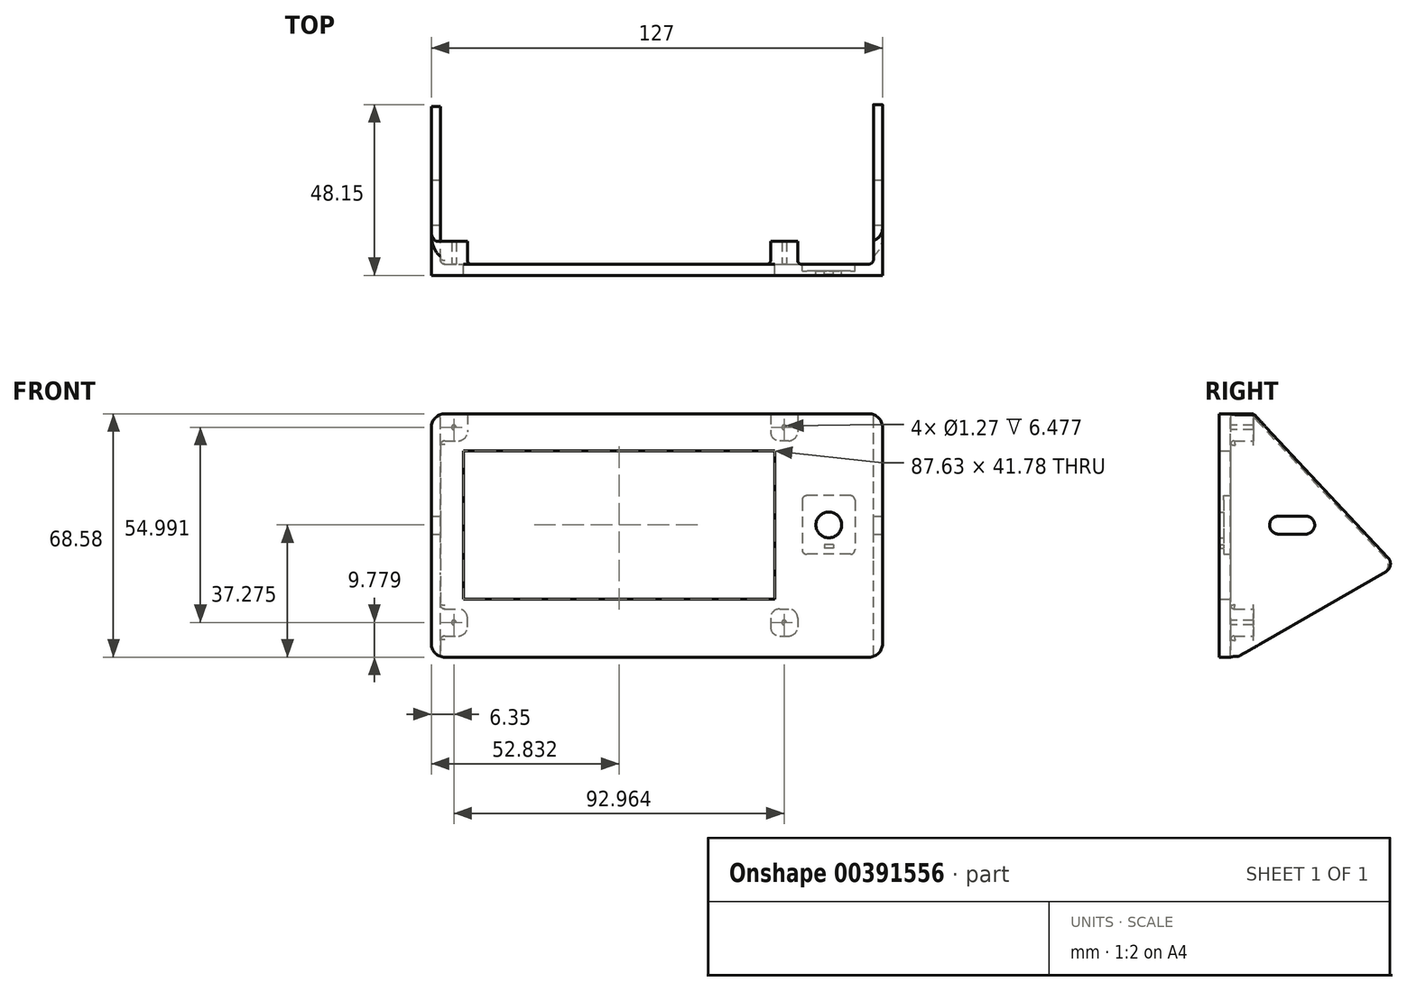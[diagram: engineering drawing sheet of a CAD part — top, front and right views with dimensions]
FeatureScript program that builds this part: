
annotation { "Feature Type Name" : "Feature", "Feature Type Description" : "" }
export const myFeature = defineFeature(function(context is Context, id is Id, definition is map)
    precondition{}
    {
        {
            var Q0;
            Q0=qCreatedBy(makeId("Front.planeOp"),FACE);
            var sketch = newSketch(context, id + "F0", { "sketchPlane" : qUnion([Q0])});
            skLineSegment(sketch, "E0.bottom", {"start": v(5.08, 2.54) * mm, "end": v(127, 2.54) * mm});
            skLineSegment(sketch, "E0.top", {"start": v(5.08, 71.12) * mm, "end": v(127, 71.12) * mm});
            skLineSegment(sketch, "E0.left", {"start": v(2.54, 5.08) * mm, "end": v(2.54, 68.58) * mm});
            skLineSegment(sketch, "E0.right", {"start": v(129.54, 5.08) * mm, "end": v(129.54, 68.58) * mm});
            skPoint(sketch, "E1.visualSharp", {"position": v(2.54, 2.54) * mm});
            skArc(sketch, "E1.filletArc", {"start": v(2.54, 5.08) * mm, "mid": v(3.28, 3.28) * mm, "end": v(5.08, 2.54) * mm});
            skPoint(sketch, "E2.visualSharp", {"position": v(2.54, 71.12) * mm});
            skArc(sketch, "E2.filletArc", {"start": v(5.08, 71.12) * mm, "mid": v(3.28, 70.38) * mm, "end": v(2.54, 68.58) * mm});
            skPoint(sketch, "E3.visualSharp", {"position": v(129.54, 71.12) * mm});
            skArc(sketch, "E3.filletArc", {"start": v(129.54, 68.58) * mm, "mid": v(128.8, 70.38) * mm, "end": v(127, 71.12) * mm});
            skPoint(sketch, "E4.visualSharp", {"position": v(129.54, 2.54) * mm});
            skArc(sketch, "E4.filletArc", {"start": v(127, 2.54) * mm, "mid": v(128.8, 3.28) * mm, "end": v(129.54, 5.08) * mm});
            skSolve(sketch);
        }
        {
            var Q0;
            Q0 = qSketchRegion(id + "F0", true);
            extrude(context, id + "F1", {"entities" : qUnion([Q0]), "oppositeDirection" : true, "depth" : 3.17 * mm, "offsetDistance" : 25.4 * mm});
        }
        {
            var Q0;
            Q0=makeQuery(id+"F1.opExtrude","CAP_FACE",FACE,{"disambiguationData":[OSD([sQuery(id+"F0.wireOp",EDGE,"E0.bottom"),sQuery(id+"F0.wireOp",EDGE,"E0.top"),sQuery(id+"F0.wireOp",EDGE,"E0.left"),sQuery(id+"F0.wireOp",EDGE,"E0.right")])],"isStart":false});
            var sketch = newSketch(context, id + "F2", { "sketchPlane" : qUnion([Q0])});
            skLineSegment(sketch, "E5.bottom", {"start": v(-5.08, 71.12) * mm, "end": v(-12.7, 71.12) * mm});
            skLineSegment(sketch, "E5.top", {"start": v(-2.54, 63.5) * mm, "end": v(-10.16, 63.5) * mm});
            skLineSegment(sketch, "E5.left", {"start": v(-2.54, 68.58) * mm, "end": v(-2.54, 63.5) * mm});
            skLineSegment(sketch, "E5.right", {"start": v(-12.7, 71.12) * mm, "end": v(-12.7, 66.04) * mm});
            skLineSegment(sketch, "E6.bottom", {"start": v(-105.66, 71.12) * mm, "end": v(-98.04, 71.12) * mm});
            skLineSegment(sketch, "E6.top", {"start": v(-103.12, 63.5) * mm, "end": v(-100.58, 63.5) * mm});
            skLineSegment(sketch, "E6.left", {"start": v(-105.66, 71.12) * mm, "end": v(-105.66, 66.04) * mm});
            skLineSegment(sketch, "E6.right", {"start": v(-98.04, 71.12) * mm, "end": v(-98.04, 66.04) * mm});
            skLineSegment(sketch, "E7.bottom", {"start": v(-2.54, 8.5) * mm, "end": v(-10.16, 8.5) * mm});
            skLineSegment(sketch, "E7.top", {"start": v(-2.54, 16.13) * mm, "end": v(-10.16, 16.13) * mm});
            skLineSegment(sketch, "E7.left", {"start": v(-2.54, 8.5) * mm, "end": v(-2.54, 16.13) * mm});
            skLineSegment(sketch, "E7.right", {"start": v(-12.7, 11.05) * mm, "end": v(-12.7, 13.59) * mm});
            skLineSegment(sketch, "E8.bottom", {"start": v(-100.58, 16.13) * mm, "end": v(-103.12, 16.13) * mm});
            skLineSegment(sketch, "E8.top", {"start": v(-100.58, 8.5) * mm, "end": v(-103.12, 8.5) * mm});
            skLineSegment(sketch, "E8.left", {"start": v(-98.04, 13.59) * mm, "end": v(-98.04, 11.05) * mm});
            skLineSegment(sketch, "E8.right", {"start": v(-105.66, 13.59) * mm, "end": v(-105.66, 11.05) * mm});
            skCircle(sketch, "E9", {"center": v(-8.89, 67.31) * mm, "radius": 0.64 * mm});
            skCircle(sketch, "E10", {"center": v(-101.85, 67.31) * mm, "radius": 0.64 * mm});
            skCircle(sketch, "E11", {"center": v(-101.85, 12.32) * mm, "radius": 0.64 * mm});
            skCircle(sketch, "E12", {"center": v(-8.89, 12.32) * mm, "radius": 0.64 * mm});
            skPoint(sketch, "E13.visualSharp", {"position": v(-2.54, 71.12) * mm});
            skArc(sketch, "E13.filletArc", {"start": v(-2.54, 68.58) * mm, "mid": v(-3.28, 70.38) * mm, "end": v(-5.08, 71.12) * mm});
            skPoint(sketch, "E14.visualSharp", {"position": v(-12.7, 63.5) * mm});
            skArc(sketch, "E14.filletArc", {"start": v(-12.7, 66.04) * mm, "mid": v(-11.96, 64.24) * mm, "end": v(-10.16, 63.5) * mm});
            skPoint(sketch, "E15.visualSharp", {"position": v(-105.66, 63.5) * mm});
            skArc(sketch, "E15.filletArc", {"start": v(-105.66, 66.04) * mm, "mid": v(-104.92, 64.24) * mm, "end": v(-103.12, 63.5) * mm});
            skPoint(sketch, "E16.visualSharp", {"position": v(-98.04, 63.5) * mm});
            skArc(sketch, "E16.filletArc", {"start": v(-100.58, 63.5) * mm, "mid": v(-98.79, 64.24) * mm, "end": v(-98.04, 66.04) * mm});
            skPoint(sketch, "E17.visualSharp", {"position": v(-98.04, 16.13) * mm});
            skArc(sketch, "E17.filletArc", {"start": v(-98.04, 13.59) * mm, "mid": v(-98.79, 15.39) * mm, "end": v(-100.58, 16.13) * mm});
            skPoint(sketch, "E18.visualSharp", {"position": v(-98.04, 8.5) * mm});
            skArc(sketch, "E18.filletArc", {"start": v(-100.58, 8.5) * mm, "mid": v(-98.79, 9.25) * mm, "end": v(-98.04, 11.05) * mm});
            skPoint(sketch, "E19.visualSharp", {"position": v(-105.66, 8.5) * mm});
            skArc(sketch, "E19.filletArc", {"start": v(-105.66, 11.05) * mm, "mid": v(-104.92, 9.25) * mm, "end": v(-103.12, 8.5) * mm});
            skPoint(sketch, "E20.visualSharp", {"position": v(-105.66, 16.13) * mm});
            skArc(sketch, "E20.filletArc", {"start": v(-103.12, 16.13) * mm, "mid": v(-104.92, 15.39) * mm, "end": v(-105.66, 13.59) * mm});
            skPoint(sketch, "E21.visualSharp", {"position": v(-12.7, 8.5) * mm});
            skArc(sketch, "E21.filletArc", {"start": v(-12.7, 11.05) * mm, "mid": v(-11.96, 9.25) * mm, "end": v(-10.16, 8.5) * mm});
            skPoint(sketch, "E22.visualSharp", {"position": v(-12.7, 16.13) * mm});
            skArc(sketch, "E22.filletArc", {"start": v(-10.16, 16.13) * mm, "mid": v(-11.96, 15.39) * mm, "end": v(-12.7, 13.59) * mm});
            skSolve(sketch);
        }
        {
            var Q0;
            Q0 = qSketchRegion(id + "F2", true);
            extrude(context, id + "F3", {"entities" : qUnion([Q0]), "operationType" : NewBodyOperationType.ADD, "depth" : 6.48 * mm, "offsetDistance" : 25.4 * mm});
        }
        {
            var Q0;
            Q0=makeQuery(id+"F3.boolean.opBoolean","MERGE",FACE,{"derivedFrom":[makeQuery(id+"F1.opExtrude","SWEPT_FACE",FACE,{"disambiguationData":[OSD([sQuery(id+"F0.wireOp",EDGE,"E0.left")])]}),makeQuery(id+"F3.opExtrude","SWEPT_FACE",FACE,{"disambiguationData":[OSD([sQuery(id+"F2.wireOp",EDGE,"E5.left")])]}),makeQuery(id+"F3.opExtrude","SWEPT_FACE",FACE,{"disambiguationData":[OSD([sQuery(id+"F2.wireOp",EDGE,"E7.left")])]})]});
            var sketch = newSketch(context, id + "F4", { "sketchPlane" : qUnion([Q0])});
            skLineSegment(sketch, "E23", {"start": v(0, 2.54) * mm, "end": v(-5.08, 2.54) * mm});
            skLineSegment(sketch, "E24", {"start": v(-5.08, 2.54) * mm, "end": v(-46.3, 26.34) * mm});
            skLineSegment(sketch, "E25", {"start": v(-46.9, 30.28) * mm, "end": v(-8.76, 71.12) * mm});
            skLineSegment(sketch, "E26", {"start": v(0, 71.12) * mm, "end": v(0, 2.54) * mm});
            skPoint(sketch, "E27.visualSharp", {"position": v(-49.07, 27.94) * mm});
            skArc(sketch, "E27.filletArc", {"start": v(-46.9, 30.28) * mm, "mid": v(-47.55, 28.17) * mm, "end": v(-46.3, 26.34) * mm});
            skLineSegment(sketch, "E28", {"start": v(-8.76, 71.12) * mm, "end": v(0, 71.12) * mm});
            skSolve(sketch);
        }
        {
            var Q0;
            Q0 = qSketchRegion(id + "F4", true);
            extrude(context, id + "F5", {"entities" : qUnion([Q0]), "operationType" : NewBodyOperationType.ADD, "oppositeDirection" : true, "depth" : 2.54 * mm, "offsetDistance" : 25.4 * mm});
        }
        {
            var Q0;
            Q0=makeQuery(id+"F1.opExtrude","SWEPT_FACE",FACE,{"disambiguationData":[OSD([sQuery(id+"F0.wireOp",EDGE,"E0.right")])]});
            var sketch = newSketch(context, id + "F6", { "sketchPlane" : qUnion([Q0])});
            skLineSegment(sketch, "E29", {"start": v(0, 2.54) * mm, "end": v(5.08, 2.54) * mm});
            skPoint(sketch, "E29.startSnap0", {"position": v(1.59, 5.08) * mm});
            skLineSegment(sketch, "E30", {"start": v(5.08, 2.54) * mm, "end": v(46.88, 26.68) * mm});
            skLineSegment(sketch, "E31", {"start": v(47.47, 30.6) * mm, "end": v(9.65, 71.12) * mm});
            skLineSegment(sketch, "E32", {"start": v(9.65, 71.12) * mm, "end": v(0, 71.12) * mm});
            skLineSegment(sketch, "E33", {"start": v(0, 71.12) * mm, "end": v(0, 2.54) * mm});
            skPoint(sketch, "E34.visualSharp", {"position": v(49.65, 28.27) * mm});
            skArc(sketch, "E34.filletArc", {"start": v(46.88, 26.68) * mm, "mid": v(48.13, 28.5) * mm, "end": v(47.47, 30.6) * mm});
            skSolve(sketch);
        }
        {
            var Q0;
            Q0 = qSketchRegion(id + "F6", true);
            extrude(context, id + "F7", {"entities" : qUnion([Q0]), "operationType" : NewBodyOperationType.ADD, "oppositeDirection" : true, "depth" : 2.54 * mm, "offsetDistance" : 25.4 * mm});
        }
        {
            var Q0;
            {var subQ0=sQuery(id+"F0.wireOp",EDGE,"E0.top");var subQ1=sQuery(id+"F0.wireOp",EDGE,"E0.right");var subQ2=sQuery(id+"F0.wireOp",EDGE,"E0.bottom");var subQ3=sQuery(id+"F0.wireOp",EDGE,"E1.filletArc");var subQ4=sQuery(id+"F0.wireOp",EDGE,"E3.filletArc");var subQ5=sQuery(id+"F0.wireOp",EDGE,"E4.filletArc");var subQ6=sQuery(id+"F0.wireOp",EDGE,"E0.left");Q0=makeQuery(id+"F3.boolean.opBoolean","SPLIT",FACE,{"disambiguationData":[TD([makeQuery(id+"F1.opExtrude","SWEPT_FACE",FACE,{"disambiguationData":[OSD([subQ2])]})])],"derivedFrom":makeQuery(id+"F1.opExtrude","CAP_FACE",FACE,{"disambiguationData":[OSD([subQ2,subQ0,subQ6,subQ1,subQ3,sQuery(id+"F0.wireOp",EDGE,"E2.filletArc"),subQ4,subQ5])],"isStart":false})});}
            var sketch = newSketch(context, id + "F8", { "sketchPlane" : qUnion([Q0])});
            skLineSegment(sketch, "E35.bottom", {"start": v(-99.19, 60.7) * mm, "end": v(-11.56, 60.7) * mm});
            skLineSegment(sketch, "E35.top", {"start": v(-99.19, 18.92) * mm, "end": v(-11.56, 18.92) * mm});
            skLineSegment(sketch, "E35.left", {"start": v(-99.19, 60.7) * mm, "end": v(-99.19, 18.92) * mm});
            skLineSegment(sketch, "E35.right", {"start": v(-11.56, 60.7) * mm, "end": v(-11.56, 18.92) * mm});
            skCircle(sketch, "E36", {"center": v(-114.43, 39.8) * mm, "radius": 3.62 * mm});
            skLineSegment(sketch, "E37", {"start": v(-114.43, 30.47) * mm, "end": v(-114.43, 45.35) * mm, "construction": true});
            skSolve(sketch);
        }
        {
            var Q0;
            Q0 = qSketchRegion(id + "F8", true);
            extrude(context, id + "F9", {"entities" : qUnion([Q0]), "operationType" : NewBodyOperationType.REMOVE, "endBound" : BoundingType.UP_TO_NEXT, "oppositeDirection" : true, "depth" : 25.4 * mm, "offsetDistance" : 25.4 * mm});
        }
        {
            var Q0;
            {var subQ0=sQuery(id+"F0.wireOp",EDGE,"E0.top");var subQ1=sQuery(id+"F0.wireOp",EDGE,"E0.right");var subQ2=sQuery(id+"F0.wireOp",EDGE,"E0.bottom");var subQ3=sQuery(id+"F0.wireOp",EDGE,"E1.filletArc");var subQ4=sQuery(id+"F0.wireOp",EDGE,"E3.filletArc");var subQ5=sQuery(id+"F0.wireOp",EDGE,"E4.filletArc");var subQ6=sQuery(id+"F0.wireOp",EDGE,"E0.left");Q0=makeQuery(id+"F3.boolean.opBoolean","SPLIT",FACE,{"disambiguationData":[TD([makeQuery(id+"F1.opExtrude","SWEPT_FACE",FACE,{"disambiguationData":[OSD([subQ2])]})])],"derivedFrom":makeQuery(id+"F1.opExtrude","CAP_FACE",FACE,{"disambiguationData":[OSD([subQ2,subQ0,subQ6,subQ1,subQ3,sQuery(id+"F0.wireOp",EDGE,"E2.filletArc"),subQ4,subQ5])],"isStart":false})});}
            var sketch = newSketch(context, id + "F10", { "sketchPlane" : qUnion([Q0])});
            skLineSegment(sketch, "E38.bottom", {"start": v(-120.52, 48.06) * mm, "end": v(-108.2, 48.06) * mm});
            skLineSegment(sketch, "E38.top", {"start": v(-120.52, 31.55) * mm, "end": v(-108.2, 31.55) * mm});
            skLineSegment(sketch, "E38.left", {"start": v(-121.8, 46.79) * mm, "end": v(-121.8, 32.82) * mm});
            skLineSegment(sketch, "E38.right", {"start": v(-106.93, 46.79) * mm, "end": v(-106.93, 32.82) * mm});
            skPoint(sketch, "E39.visualSharp", {"position": v(-106.93, 31.55) * mm});
            skArc(sketch, "E39.filletArc", {"start": v(-108.2, 31.55) * mm, "mid": v(-107.3, 31.92) * mm, "end": v(-106.93, 32.82) * mm});
            skPoint(sketch, "E40.visualSharp", {"position": v(-106.93, 48.06) * mm});
            skArc(sketch, "E40.filletArc", {"start": v(-106.93, 46.79) * mm, "mid": v(-107.3, 47.68) * mm, "end": v(-108.2, 48.06) * mm});
            skPoint(sketch, "E41.visualSharp", {"position": v(-121.8, 48.06) * mm});
            skArc(sketch, "E41.filletArc", {"start": v(-120.52, 48.06) * mm, "mid": v(-121.42, 47.68) * mm, "end": v(-121.8, 46.79) * mm});
            skPoint(sketch, "E42.visualSharp", {"position": v(-121.8, 31.55) * mm});
            skArc(sketch, "E42.filletArc", {"start": v(-121.8, 32.82) * mm, "mid": v(-121.42, 31.92) * mm, "end": v(-120.52, 31.55) * mm});
            skSolve(sketch);
        }
        {
            var Q0;
            Q0 = qSketchRegion(id + "F10", true);
            extrude(context, id + "F11", {"entities" : qUnion([Q0]), "operationType" : NewBodyOperationType.REMOVE, "oppositeDirection" : true, "depth" : 1.9 * mm, "offsetDistance" : 25.4 * mm});
        }
        {
            var Q0;
            Q0=makeQuery(id+"F11.boolean.opBoolean","COPY",FACE,{"derivedFrom":makeQuery(id+"F11.opExtrude","CAP_FACE",FACE,{"disambiguationData":[OSD([sQuery(id+"F10.wireOp",EDGE,"E38.bottom"),sQuery(id+"F10.wireOp",EDGE,"E38.top"),sQuery(id+"F10.wireOp",EDGE,"E38.left"),sQuery(id+"F10.wireOp",EDGE,"E38.right"),sQuery(id+"F10.wireOp",EDGE,"E39.filletArc"),sQuery(id+"F10.wireOp",EDGE,"E40.filletArc"),sQuery(id+"F10.wireOp",EDGE,"E41.filletArc"),sQuery(id+"F10.wireOp",EDGE,"E42.filletArc")])],"isStart":false})});
            var sketch = newSketch(context, id + "F12", { "sketchPlane" : qUnion([Q0])});
            skLineSegment(sketch, "E43.bottom", {"start": v(-115.7, 34.28) * mm, "end": v(-113.16, 34.28) * mm});
            skLineSegment(sketch, "E43.top", {"start": v(-115.7, 33.27) * mm, "end": v(-113.16, 33.27) * mm});
            skLineSegment(sketch, "E43.left", {"start": v(-115.7, 34.28) * mm, "end": v(-115.7, 33.27) * mm});
            skLineSegment(sketch, "E43.right", {"start": v(-113.16, 34.28) * mm, "end": v(-113.16, 33.27) * mm});
            skSolve(sketch);
        }
        {
            var Q0;
            Q0 = qSketchRegion(id + "F12", true);
            extrude(context, id + "F13", {"entities" : qUnion([Q0]), "operationType" : NewBodyOperationType.REMOVE, "oppositeDirection" : true, "depth" : 1.02 * mm, "offsetDistance" : 25.4 * mm});
        }
        {
            var Q0;
            Q0=makeQuery(id+"F7.boolean.opBoolean","MERGE",FACE,{"derivedFrom":[makeQuery(id+"F1.opExtrude","SWEPT_FACE",FACE,{"disambiguationData":[OSD([sQuery(id+"F0.wireOp",EDGE,"E0.right")])]}),makeQuery(id+"F7.opExtrude","CAP_FACE",FACE,{"disambiguationData":[OSD([sQuery(id+"F6.wireOp",EDGE,"E29"),sQuery(id+"F6.wireOp",EDGE,"E30"),sQuery(id+"F6.wireOp",EDGE,"E31"),sQuery(id+"F6.wireOp",EDGE,"E32"),sQuery(id+"F6.wireOp",EDGE,"E33"),sQuery(id+"F6.wireOp",EDGE,"E34.filletArc")])],"isStart":true})]});
            var sketch = newSketch(context, id + "F14", { "sketchPlane" : qUnion([Q0])});
            skLineSegment(sketch, "E44.bottom", {"start": v(24.3, 42.31) * mm, "end": v(16.67, 42.31) * mm});
            skLineSegment(sketch, "E44.top", {"start": v(24.3, 37.23) * mm, "end": v(16.67, 37.23) * mm});
            skLineSegment(sketch, "E44.left", {"start": v(26.83, 39.77) * mm, "end": v(26.83, 39.77) * mm});
            skLineSegment(sketch, "E44.right", {"start": v(14.13, 39.77) * mm, "end": v(14.13, 39.77) * mm});
            skPoint(sketch, "E45.visualSharp", {"position": v(26.83, 42.31) * mm});
            skArc(sketch, "E45.filletArc", {"start": v(26.83, 39.77) * mm, "mid": v(26.09, 41.57) * mm, "end": v(24.3, 42.31) * mm});
            skPoint(sketch, "E46.visualSharp", {"position": v(26.83, 37.23) * mm});
            skArc(sketch, "E46.filletArc", {"start": v(24.3, 37.23) * mm, "mid": v(26.09, 37.98) * mm, "end": v(26.83, 39.77) * mm});
            skPoint(sketch, "E47.visualSharp", {"position": v(14.13, 37.23) * mm});
            skArc(sketch, "E47.filletArc", {"start": v(14.13, 39.77) * mm, "mid": v(14.88, 37.98) * mm, "end": v(16.67, 37.23) * mm});
            skPoint(sketch, "E48.visualSharp", {"position": v(14.13, 42.31) * mm});
            skArc(sketch, "E48.filletArc", {"start": v(16.67, 42.31) * mm, "mid": v(14.88, 41.57) * mm, "end": v(14.13, 39.77) * mm});
            skSolve(sketch);
        }
        {
            var Q0;
            Q0 = qSketchRegion(id + "F14", true);
            extrude(context, id + "F15", {"entities" : qUnion([Q0]), "operationType" : NewBodyOperationType.REMOVE, "endBound" : BoundingType.THROUGH_ALL, "oppositeDirection" : true, "depth" : 25.4 * mm, "offsetDistance" : 25.4 * mm});
        }
        {
            var Q0;
            Q0=makeQuery(id+"F5.opExtrude","CAP_EDGE",EDGE,{"disambiguationData":[OSD([sQuery(id+"F4.wireOp",EDGE,"E28")])],"isStart":true});
            var Q1;
            Q1=makeQuery(id+"F5.opExtrude","CAP_EDGE",EDGE,{"disambiguationData":[OSD([sQuery(id+"F4.wireOp",EDGE,"E23")])],"isStart":true});
            var Q2;
            Q2=makeQuery(id+"F7.opExtrude","CAP_EDGE",EDGE,{"disambiguationData":[OSD([sQuery(id+"F6.wireOp",EDGE,"E32")])],"isStart":true});
            var Q3;
            Q3=makeQuery(id+"F7.opExtrude","CAP_EDGE",EDGE,{"disambiguationData":[OSD([sQuery(id+"F6.wireOp",EDGE,"E29")])],"isStart":true});
            fillet(context, id + "F16", {"entities" : qUnion([Q0, Q1, Q2, Q3]), "radius" : 3.8 * mm, "tangentPropagation" : true, "allowEdgeOverflow" : false});
        }
        {
            var Q0;
            Q0=makeQuery(id+"F3.opExtrude","CAP_EDGE",EDGE,{"disambiguationData":[OSD([sQuery(id+"F2.wireOp",EDGE,"E8.top")])],"isStart":true});
            var Q1;
            Q1=makeQuery(id+"F3.opExtrude","CAP_EDGE",EDGE,{"disambiguationData":[OSD([sQuery(id+"F2.wireOp",EDGE,"E15.filletArc")])],"isStart":true});
            var Q2;
            Q2=makeQuery(id+"F3.opExtrude","CAP_EDGE",EDGE,{"disambiguationData":[OSD([sQuery(id+"F2.wireOp",EDGE,"E7.bottom")])],"isStart":true});
            var Q3;
            Q3=makeQuery(id+"F3.opExtrude","CAP_EDGE",EDGE,{"disambiguationData":[OSD([sQuery(id+"F2.wireOp",EDGE,"E5.top")])],"isStart":true});
            fillet(context, id + "F17", {"entities" : qUnion([Q0, Q1, Q2, Q3]), "radius" : 1.02 * mm, "tangentPropagation" : true, "allowEdgeOverflow" : false});
        }
        {
            var Q0;
            {var subQ0=sQuery(id+"F0.wireOp",EDGE,"E0.top");var subQ1=sQuery(id+"F0.wireOp",EDGE,"E0.right");var subQ2=sQuery(id+"F0.wireOp",EDGE,"E0.bottom");var subQ3=sQuery(id+"F0.wireOp",EDGE,"E1.filletArc");var subQ4=sQuery(id+"F0.wireOp",EDGE,"E3.filletArc");var subQ5=sQuery(id+"F0.wireOp",EDGE,"E4.filletArc");var subQ6=sQuery(id+"F0.wireOp",EDGE,"E0.left");Q0=makeQuery(id+"F5.boolean.opBoolean","INTERSECT",EDGE,{"disambiguationData":[OD(1.0)],"derivedFrom":[makeQuery(id+"F3.boolean.opBoolean","SPLIT",FACE,{"disambiguationData":[TD([makeQuery(id+"F1.opExtrude","SWEPT_FACE",FACE,{"disambiguationData":[OSD([subQ2])]})])],"derivedFrom":makeQuery(id+"F1.opExtrude","CAP_FACE",FACE,{"disambiguationData":[OSD([subQ2,subQ0,subQ6,subQ1,subQ3,sQuery(id+"F0.wireOp",EDGE,"E2.filletArc"),subQ4,subQ5])],"isStart":false})}),makeQuery(id+"F5.opExtrude","CAP_FACE",FACE,{"disambiguationData":[OSD([sQuery(id+"F4.wireOp",EDGE,"E23"),sQuery(id+"F4.wireOp",EDGE,"E24"),sQuery(id+"F4.wireOp",EDGE,"E25"),sQuery(id+"F4.wireOp",EDGE,"E26"),sQuery(id+"F4.wireOp",EDGE,"E27.filletArc"),sQuery(id+"F4.wireOp",EDGE,"E28")])],"isStart":false})]});}
            var Q1;
            {var subQ0=sQuery(id+"F0.wireOp",EDGE,"E0.top");var subQ1=sQuery(id+"F0.wireOp",EDGE,"E0.right");var subQ2=sQuery(id+"F0.wireOp",EDGE,"E0.bottom");var subQ3=sQuery(id+"F0.wireOp",EDGE,"E1.filletArc");var subQ4=sQuery(id+"F0.wireOp",EDGE,"E3.filletArc");var subQ5=sQuery(id+"F0.wireOp",EDGE,"E4.filletArc");var subQ6=sQuery(id+"F0.wireOp",EDGE,"E0.left");Q1=makeQuery(id+"F7.boolean.opBoolean","INTERSECT",EDGE,{"derivedFrom":[makeQuery(id+"F3.boolean.opBoolean","SPLIT",FACE,{"disambiguationData":[TD([makeQuery(id+"F1.opExtrude","SWEPT_FACE",FACE,{"disambiguationData":[OSD([subQ2])]})])],"derivedFrom":makeQuery(id+"F1.opExtrude","CAP_FACE",FACE,{"disambiguationData":[OSD([subQ2,subQ0,subQ6,subQ1,subQ3,sQuery(id+"F0.wireOp",EDGE,"E2.filletArc"),subQ4,subQ5])],"isStart":false})}),makeQuery(id+"F7.opExtrude","CAP_FACE",FACE,{"disambiguationData":[OSD([sQuery(id+"F6.wireOp",EDGE,"E29"),sQuery(id+"F6.wireOp",EDGE,"E30"),sQuery(id+"F6.wireOp",EDGE,"E31"),sQuery(id+"F6.wireOp",EDGE,"E32"),sQuery(id+"F6.wireOp",EDGE,"E33"),sQuery(id+"F6.wireOp",EDGE,"E34.filletArc")])],"isStart":false})]});}
            fillet(context, id + "F18", {"entities" : qUnion([Q0, Q1]), "radius" : 1.27 * mm, "tangentPropagation" : true, "allowEdgeOverflow" : false});
        }
    });
